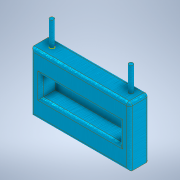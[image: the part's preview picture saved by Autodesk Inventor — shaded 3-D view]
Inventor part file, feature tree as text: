
AUTODESK INVENTOR PART (.ipt)
format: ipt  version: 2021.3 (Build 253353000, 353)  size: 184,832 bytes
history: native  units: mm
features: sketch x5, extrude x4, fillet x1
ambient origin geometry x8: Origin, YZ Plane, XZ Plane, XY Plane, X Axis, Y Axis, Z Axis, Center Point
bodies: Solid1 (feature_tree)
feature tree (10):
  extrude  "Extrusion1"  Depth=15.0mm TaperAngle=0.0deg
  extrude  "Extrusion2"  Depth=25.0mm TaperAngle=0.0deg
  extrude  "Extrusion3"  Depth=3.0mm
  extrude  "Extrusion4"  [1 undecoded]
  sketch  "Sketch5"
  fillet  "Fillet1"  [1 undecoded]
  sketch  "Sketch1"  dims[d2=20.0mm d3=0.0mm d8=15.0mm d9=0.0mm]
  sketch  "Sketch2"  dims[d10=0.0mm d11=0.0mm d16=25.0mm d17=0.0mm]
  sketch  "Sketch3"  dims[d18=80.0mm d19=3.0mm]
  sketch  "Sketch4"
note: 2 required parameter values undecoded (feature->parameter linkage not recoverable at this tier; creation-order binding heuristic only, values carry confidence <= 0.55)
